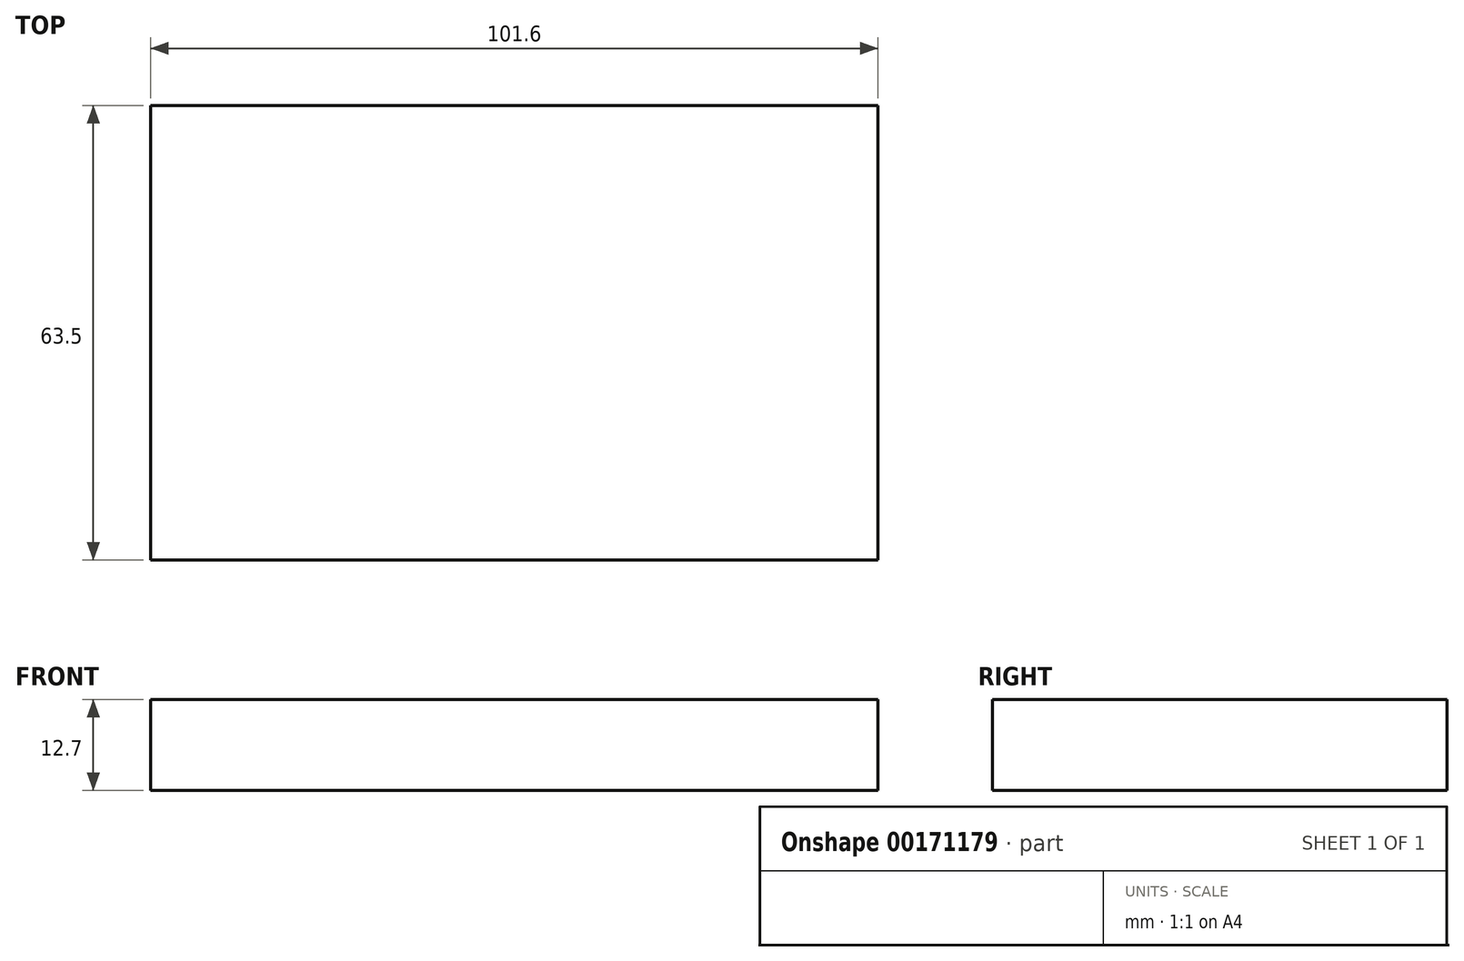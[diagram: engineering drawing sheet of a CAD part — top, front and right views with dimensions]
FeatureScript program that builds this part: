
annotation { "Feature Type Name" : "Feature", "Feature Type Description" : "" }
export const myFeature = defineFeature(function(context is Context, id is Id, definition is map)
    precondition{}
    {
        {
            var Q0;
            Q0=qCreatedBy(makeId("Top.planeOp"),FACE);
            var sketch = newSketch(context, id + "F0", { "sketchPlane" : qUnion([Q0])});
            skLineSegment(sketch, "E0.bottom", {"start": v(50.8, 31.75) * mm, "end": v(-50.8, 31.75) * mm});
            skLineSegment(sketch, "E0.top", {"start": v(50.8, -31.75) * mm, "end": v(-50.8, -31.75) * mm});
            skLineSegment(sketch, "E0.left", {"start": v(50.8, 31.75) * mm, "end": v(50.8, -31.75) * mm});
            skLineSegment(sketch, "E0.right", {"start": v(-50.8, 31.75) * mm, "end": v(-50.8, -31.75) * mm});
            skPoint(sketch, "E0.middle", {"position": v(0, 0) * mm});
            skSolve(sketch);
        }
        {
            var Q0;
            Q0=makeQuery(id+"F0.imprint","IMPRINT",FACE,{"disambiguationData":[TD([[makeQuery(id+"F0.imprint","IMPRINT",EDGE,{"derivedFrom":sQuery(id+"F0.wireOp",EDGE,"E0.bottom")}),1.0]])]});
            extrude(context, id + "F1", {"entities" : qUnion([Q0]), "depth" : 12.7 * mm});
        }
    });
